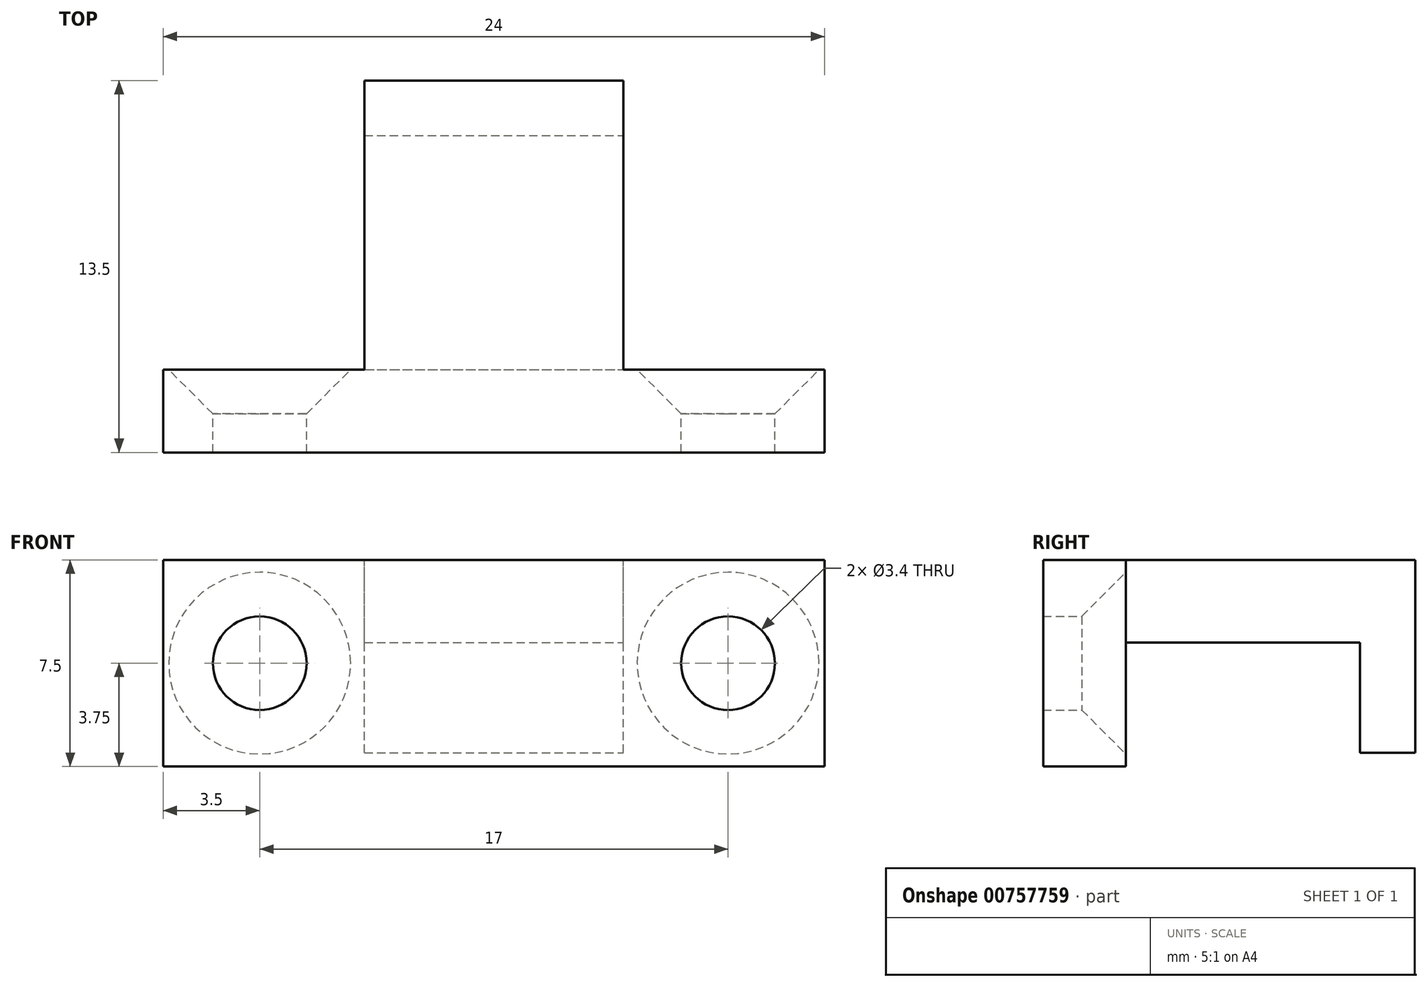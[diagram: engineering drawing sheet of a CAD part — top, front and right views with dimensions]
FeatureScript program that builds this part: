
annotation { "Feature Type Name" : "Feature", "Feature Type Description" : "" }
export const myFeature = defineFeature(function(context is Context, id is Id, definition is map)
    precondition{}
    {
        {
            var Q0;
            Q0=qCreatedBy(makeId("Front.planeOp"),FACE);
            var sketch = newSketch(context, id + "F0", { "sketchPlane" : qUnion([Q0])});
            skLineSegment(sketch, "E0.bottom", {"start": v(-12, 3.75) * mm, "end": v(12, 3.75) * mm});
            skLineSegment(sketch, "E0.top", {"start": v(-12, -3.75) * mm, "end": v(12, -3.75) * mm});
            skLineSegment(sketch, "E0.left", {"start": v(-12, 3.75) * mm, "end": v(-12, -3.75) * mm});
            skLineSegment(sketch, "E0.right", {"start": v(12, 3.75) * mm, "end": v(12, -3.75) * mm});
            skPoint(sketch, "E0.middle", {"position": v(0, 0) * mm});
            skPoint(sketch, "E1", {"position": v(-8.5, 0) * mm});
            skPoint(sketch, "E2", {"position": v(8.5, 0) * mm});
            skSolve(sketch);
        }
        {
            var Q0;
            Q0=makeQuery(id+"F0.imprint","IMPRINT",FACE,{"disambiguationData":[TD([[makeQuery(id+"F0.imprint","IMPRINT",EDGE,{"derivedFrom":sQuery(id+"F0.wireOp",EDGE,"E0.bottom")}),-1.0]])]});
            extrude(context, id + "F1", {"entities" : qUnion([Q0]), "depth" : 3 * mm, "offsetDistance" : 25 * mm});
        }
        {
            var Q0;
            Q0=sQuery(id+"F0.wireOp",VERTEX,"E1");
            var Q1;
            Q1=sQuery(id+"F0.wireOp",VERTEX,"E2");
            var Q2;
            Q2=makeQuery(id+"F1.opExtrude","SWEPT_BODY",BODY,{"disambiguationData":[OSD([sQuery(id+"F0.wireOp",EDGE,"E0.bottom"),sQuery(id+"F0.wireOp",EDGE,"E0.top"),sQuery(id+"F0.wireOp",EDGE,"E0.left"),sQuery(id+"F0.wireOp",EDGE,"E0.right")])]});
            hole(context, id + "F2", {"style" : HoleStyle.C_SINK, "endStyle" : HoleEndStyle.THROUGH, "oppositeDirection" : true, "holeDiameter" : 3.4 * mm, "cSinkDiameter" : 6.6 * mm, "cSinkAngle" : 90 * degree, "majorDiameter" : 5 * mm, "isTappedThrough" : true, "tappedDepth" : 12 * mm, "tapClearance" : 3, "startFromSketch" : true, "locations" : qUnion([Q0, Q1]), "scope" : qUnion([Q2])});
        }
        {
            var Q0;
            Q0=makeQuery(id+"F0.imprint","IMPRINT",FACE,{"disambiguationData":[TD([[makeQuery(id+"F0.imprint","IMPRINT",EDGE,{"derivedFrom":sQuery(id+"F0.wireOp",EDGE,"E0.bottom")}),-1.0]])]});
            var sketch = newSketch(context, id + "F3", { "sketchPlane" : qUnion([Q0])});
            skLineSegment(sketch, "E3.bottom", {"start": v(-4.7, -3.75) * mm, "end": v(4.7, -3.75) * mm});
            skLineSegment(sketch, "E3.top", {"start": v(-4.7, 3.75) * mm, "end": v(4.7, 3.75) * mm});
            skLineSegment(sketch, "E3.left", {"start": v(-4.7, -3.75) * mm, "end": v(-4.7, 3.75) * mm});
            skLineSegment(sketch, "E3.right", {"start": v(4.7, -3.75) * mm, "end": v(4.7, 3.75) * mm});
            skPoint(sketch, "E3.middle", {"position": v(0, 0) * mm});
            skLineSegment(sketch, "E4.top", {"start": v(-4.7, 0.75) * mm, "end": v(4.7, 0.75) * mm});
            skLineSegment(sketch, "E4.left", {"start": v(-4.7, 3.75) * mm, "end": v(-4.7, 0.75) * mm});
            skLineSegment(sketch, "E4.right", {"start": v(4.7, 3.75) * mm, "end": v(4.7, 0.75) * mm});
            skSolve(sketch);
        }
        {
            var Q0;
            Q0=makeQuery(id+"F3.imprint","IMPRINT",FACE,{"disambiguationData":[TD([[makeQuery(id+"F3.imprint","IMPRINT",EDGE,{"derivedFrom":sQuery(id+"F3.wireOp",EDGE,"E3.top")}),-1.0]])]});
            extrude(context, id + "F4", {"entities" : qUnion([Q0]), "operationType" : NewBodyOperationType.ADD, "oppositeDirection" : true, "depth" : 10.5 * mm, "offsetDistance" : 25 * mm});
        }
        {
            var Q0;
            Q0=makeQuery(id+"F4.opExtrude","SWEPT_FACE",FACE,{"disambiguationData":[OSD([sQuery(id+"F3.wireOp",EDGE,"E4.top")])]});
            var sketch = newSketch(context, id + "F5", { "sketchPlane" : qUnion([Q0])});
            skLineSegment(sketch, "E5.bottom", {"start": v(-4.7, -10.5) * mm, "end": v(4.7, -10.5) * mm});
            skLineSegment(sketch, "E5.top", {"start": v(-4.7, -8.5) * mm, "end": v(4.7, -8.5) * mm});
            skLineSegment(sketch, "E5.left", {"start": v(-4.7, -10.5) * mm, "end": v(-4.7, -8.5) * mm});
            skLineSegment(sketch, "E5.right", {"start": v(4.7, -10.5) * mm, "end": v(4.7, -8.5) * mm});
            skSolve(sketch);
        }
        {
            var Q0;
            Q0=makeQuery(id+"F5.imprint","IMPRINT",FACE,{"disambiguationData":[TD([[makeQuery(id+"F5.imprint","IMPRINT",EDGE,{"derivedFrom":sQuery(id+"F5.wireOp",EDGE,"E5.bottom")}),1.0]])]});
            extrude(context, id + "F6", {"entities" : qUnion([Q0]), "operationType" : NewBodyOperationType.ADD, "depth" : 4 * mm, "offsetDistance" : 25 * mm});
        }
    });
